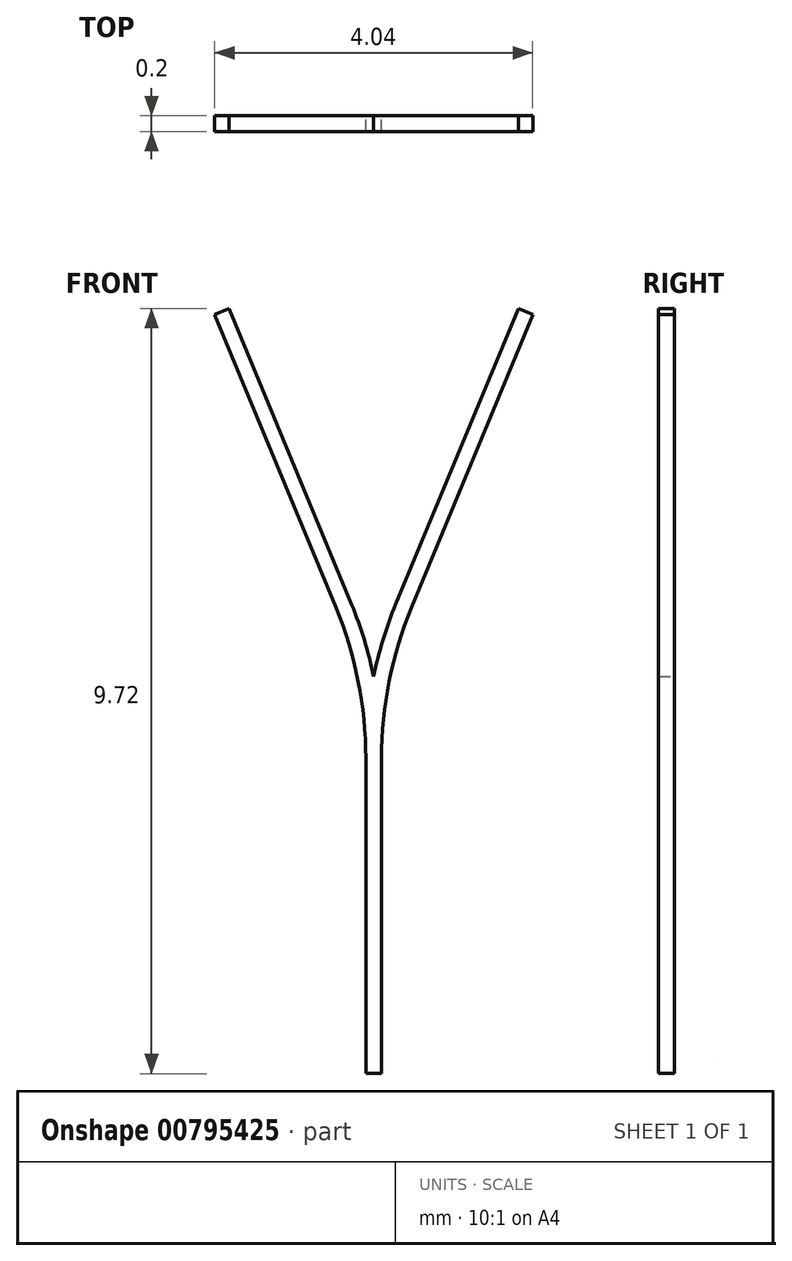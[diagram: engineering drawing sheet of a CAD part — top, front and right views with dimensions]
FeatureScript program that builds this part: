
annotation { "Feature Type Name" : "Feature", "Feature Type Description" : "" }
export const myFeature = defineFeature(function(context is Context, id is Id, definition is map)
    precondition{}
    {
        {
            var Q0;
            Q0=qCreatedBy(makeId("Front.planeOp"),FACE);
            var sketch = newSketch(context, id + "F0", { "sketchPlane" : qUnion([Q0])});
            skLineSegment(sketch, "E0", {"start": v(-2.02, 4.55) * mm, "end": v(-0.48, 0.83) * mm});
            skLineSegment(sketch, "E1", {"start": v(0.48, 0.83) * mm, "end": v(2.02, 4.55) * mm});
            skLineSegment(sketch, "E2.0", {"start": v(-1.84, 4.63) * mm, "end": v(-0.28, 0.87) * mm});
            skLineSegment(sketch, "E3.0", {"start": v(0.28, 0.87) * mm, "end": v(1.84, 4.63) * mm});
            skLineSegment(sketch, "E4.0", {"start": v(0.1, -1.08) * mm, "end": v(0.1, -5.09) * mm});
            skLineSegment(sketch, "E5.0", {"start": v(-0.1, -1.04) * mm, "end": v(-0.1, -5.09) * mm});
            skLineSegment(sketch, "E6", {"start": v(-0.1, -5.09) * mm, "end": v(0.1, -5.09) * mm});
            skLineSegment(sketch, "E7", {"start": v(-1.84, 4.63) * mm, "end": v(-2.02, 4.55) * mm});
            skLineSegment(sketch, "E8", {"start": v(2.02, 4.55) * mm, "end": v(1.84, 4.63) * mm});
            skPoint(sketch, "E9.visualSharp", {"position": v(-0.1, -0.09) * mm});
            skArc(sketch, "E9.filletArc", {"start": v(-0.1, -1.08) * mm, "mid": v(-0.2, -0.1) * mm, "end": v(-0.48, 0.83) * mm});
            skPoint(sketch, "E10.visualSharp", {"position": v(0.1, -0.09) * mm});
            skArc(sketch, "E10.filletArc", {"start": v(0.48, 0.83) * mm, "mid": v(0.2, -0.1) * mm, "end": v(0.1, -1.08) * mm});
            skLineSegment(sketch, "E11", {"start": v(0.1, -1.08) * mm, "end": v(0.1, -1.04) * mm});
            skArc(sketch, "E12.filletArc", {"start": v(0, -0.04) * mm, "mid": v(-0.12, 0.42) * mm, "end": v(-0.28, 0.87) * mm});
            skPoint(sketch, "E13.orphan", {"position": v(0, 0.2) * mm});
            skArc(sketch, "E14.filletArc", {"start": v(0.28, 0.87) * mm, "mid": v(0.12, 0.42) * mm, "end": v(0, -0.04) * mm});
            skSolve(sketch);
        }
        {
            var Q0;
            Q0=qSketchRegion(id+"F0",true);
            extrude(context, id + "F1", {"entities" : qUnion([Q0]), "depth" : 0.2 * mm, "offsetDistance" : 25 * mm});
        }
    });
